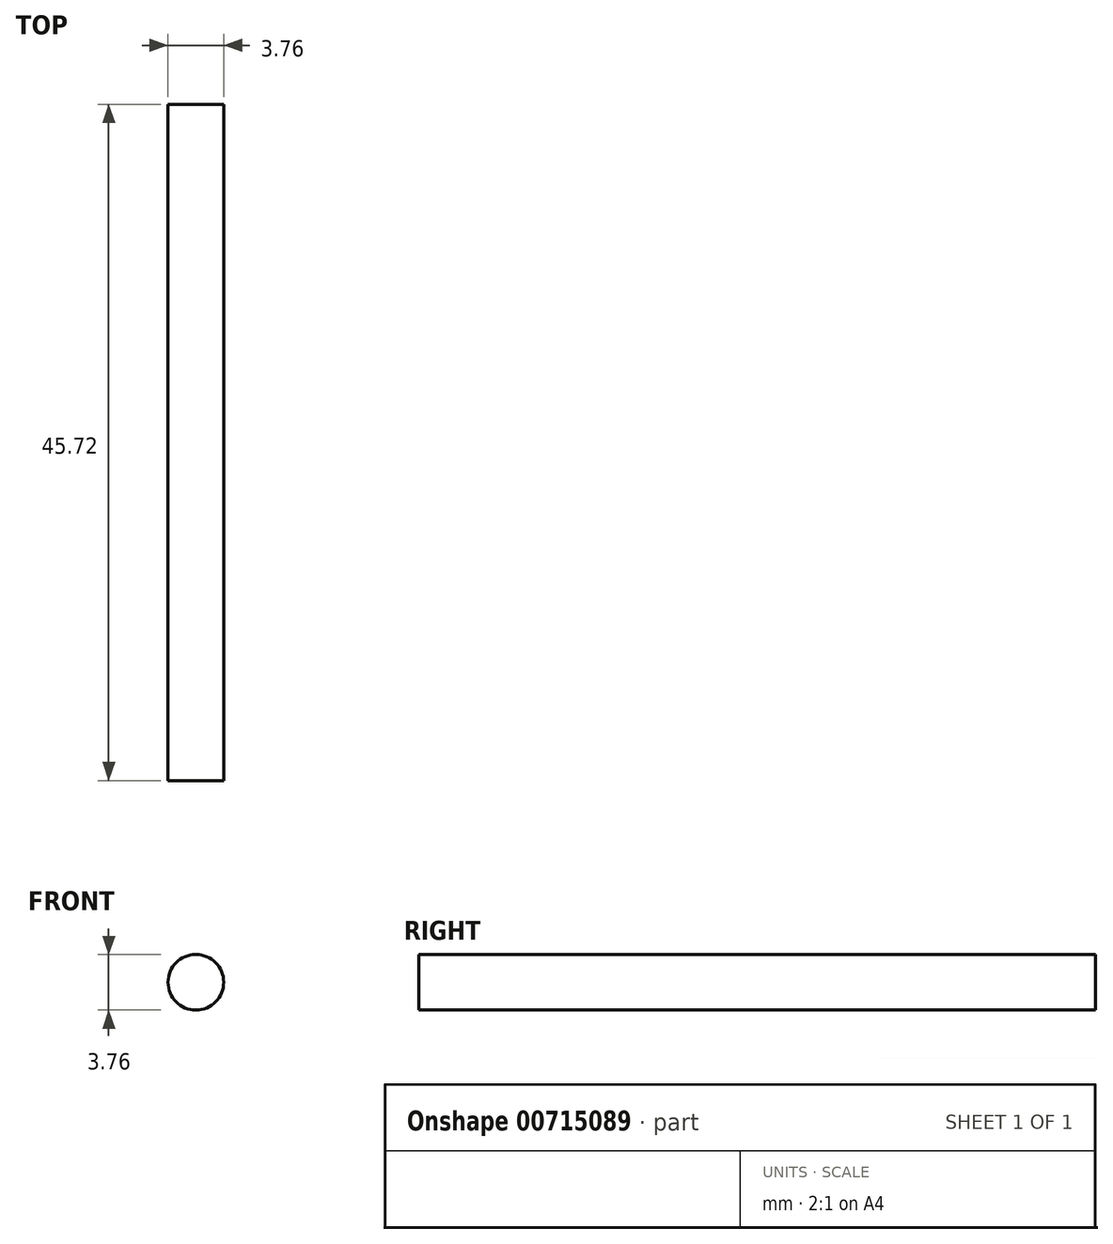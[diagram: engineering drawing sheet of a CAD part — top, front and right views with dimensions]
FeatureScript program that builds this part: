
annotation { "Feature Type Name" : "Feature", "Feature Type Description" : "" }
export const myFeature = defineFeature(function(context is Context, id is Id, definition is map)
    precondition{}
    {
        {
            var Q0;
            Q0=qCreatedBy(makeId("Front.planeOp"),FACE);
            var sketch = newSketch(context, id + "F0", { "sketchPlane" : qUnion([Q0])});
            skCircle(sketch, "E0", {"center": v(0, 0) * mm, "radius": 1.88 * mm});
            skSolve(sketch);
        }
        {
            var Q0;
            Q0=makeQuery(id+"F0.imprint","IMPRINT",FACE,{"disambiguationData":[TD([[makeQuery(id+"F0.imprint","IMPRINT",EDGE,{"derivedFrom":sQuery(id+"F0.wireOp",EDGE,"E0")}),1.0]])]});
            extrude(context, id + "F1", {"entities" : qUnion([Q0]), "depth" : 45.72 * mm, "offsetDistance" : 25.4 * mm});
        }
    });
